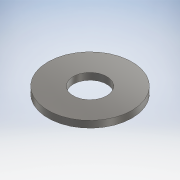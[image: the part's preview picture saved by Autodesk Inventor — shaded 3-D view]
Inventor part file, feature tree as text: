
AUTODESK INVENTOR PART (.ipt)
format: ipt  version: 2018 (Build 220112000, 112)  size: 95,744 bytes
history: native  units: mm
features: extrude x1, sketch x1
ambient origin geometry x8: Origin, YZ Plane, XZ Plane, XY Plane, X Axis, Y Axis, Z Axis, Center Point
bodies: Solid1 (feature_tree)
feature tree (2):
  extrude  "Extrusion1"  Depth=0.4mm
  sketch  "Sketch1"  dims[d0=2.0mm d1=5.0mm d2=0.4mm d3=0.0mm]
